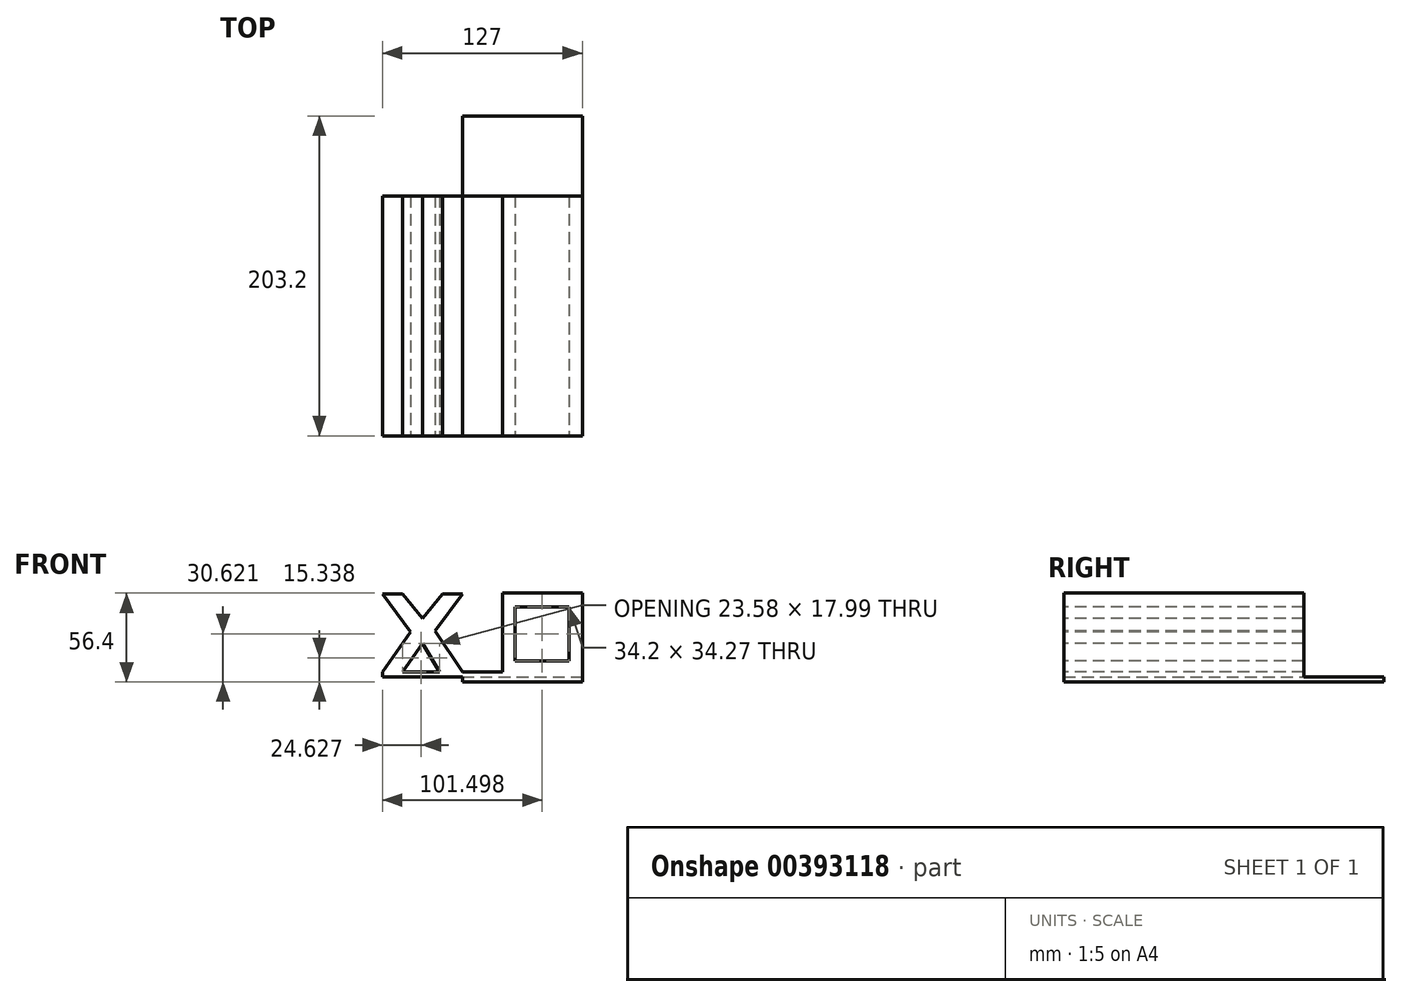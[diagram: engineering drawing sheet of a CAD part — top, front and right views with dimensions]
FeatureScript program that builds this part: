
annotation { "Feature Type Name" : "Feature", "Feature Type Description" : "" }
export const myFeature = defineFeature(function(context is Context, id is Id, definition is map)
    precondition{}
    {
        {
            var Q0;
            Q0=qCreatedBy(makeId("Top.planeOp"),FACE);
            var sketch = newSketch(context, id + "F0", { "sketchPlane" : qUnion([Q0])});
            skLineSegment(sketch, "E0.bottom", {"start": v(101.6, -101.6) * mm, "end": v(-101.6, -101.6) * mm});
            skLineSegment(sketch, "E0.top", {"start": v(101.6, 101.6) * mm, "end": v(-101.6, 101.6) * mm});
            skLineSegment(sketch, "E0.left", {"start": v(101.6, -101.6) * mm, "end": v(101.6, 101.6) * mm});
            skLineSegment(sketch, "E0.right", {"start": v(-101.6, -101.6) * mm, "end": v(-101.6, 101.6) * mm});
            skPoint(sketch, "E0.middle", {"position": v(0, 0) * mm});
            skSolve(sketch);
        }
        {
            var Q0;
            Q0=makeQuery(id+"F0.imprint","IMPRINT",FACE,{"disambiguationData":[TD([[makeQuery(id+"F0.imprint","IMPRINT",EDGE,{"derivedFrom":sQuery(id+"F0.wireOp",EDGE,"E0.bottom")}),-1.0]])]});
            extrude(context, id + "F1", {"entities" : qUnion([Q0]), "depth" : 6.35 * mm});
        }
        {
            var Q0;
            Q0=makeQuery(id+"F1.opExtrude","CAP_FACE",FACE,{"disambiguationData":[OSD([sQuery(id+"F0.wireOp",EDGE,"E0.bottom"),sQuery(id+"F0.wireOp",EDGE,"E0.top"),sQuery(id+"F0.wireOp",EDGE,"E0.left"),sQuery(id+"F0.wireOp",EDGE,"E0.right")])],"isStart":false});
            var sketch = newSketch(context, id + "F2", { "sketchPlane" : qUnion([Q0])});
            skLineSegment(sketch, "E1.bottom", {"start": v(-105.25, 101.6) * mm, "end": v(123.35, 101.6) * mm});
            skLineSegment(sketch, "E1.top", {"start": v(-105.25, 50.8) * mm, "end": v(123.35, 50.8) * mm});
            skLineSegment(sketch, "E1.left", {"start": v(-105.25, 101.6) * mm, "end": v(-105.25, 50.8) * mm});
            skLineSegment(sketch, "E1.right", {"start": v(123.35, 101.6) * mm, "end": v(123.35, 50.8) * mm});
            skSolve(sketch);
        }
        {
            var Q0;
            Q0=qSketchRegion(id+"F2",true);
            extrude(context, id + "F3", {"entities" : qUnion([Q0]), "operationType" : NewBodyOperationType.REMOVE, "oppositeDirection" : true, "depth" : 3.17 * mm});
        }
        {
            var Q0;
            Q0=qCreatedBy(makeId("Front.planeOp"),FACE);
            var sketch = newSketch(context, id + "F4", { "sketchPlane" : qUnion([Q0])});
            skLineSegment(sketch, "E2.bottom", {"start": v(101.6, 5.6) * mm, "end": v(50.8, 5.6) * mm});
            skLineSegment(sketch, "E2.top", {"start": v(101.6, 56.4) * mm, "end": v(50.8, 56.4) * mm});
            skLineSegment(sketch, "E2.left", {"start": v(101.6, 5.6) * mm, "end": v(101.6, 56.4) * mm});
            skLineSegment(sketch, "E2.right", {"start": v(50.8, 5.6) * mm, "end": v(50.8, 56.4) * mm});
            skSolve(sketch);
        }
        {
            var Q0;
            Q0=makeQuery(id+"F4.imprint","IMPRINT",FACE,{"disambiguationData":[TD([[makeQuery(id+"F4.imprint","IMPRINT",EDGE,{"derivedFrom":sQuery(id+"F4.wireOp",EDGE,"E2.bottom")}),-1.0]])]});
            extrude(context, id + "F5", {"entities" : qUnion([Q0]), "operationType" : NewBodyOperationType.ADD, "depth" : 101.6 * mm});
        }
        {
            var Q0;
            Q0=makeQuery(id+"F5.boolean.opBoolean","MERGE",FACE,{"derivedFrom":[makeQuery(id+"FEnlMJxP7i9bCVA_1.boolean.opBoolean","MERGE",FACE,{"derivedFrom":[makeQuery(id+"F2wCx2niY0FLEcg_1.boolean.opBoolean","MERGE",FACE,{"derivedFrom":[makeQuery(id+"F1.opExtrude","SWEPT_FACE",FACE,{"disambiguationData":[OSD([sQuery(id+"F0.wireOp",EDGE,"E0.bottom")])]}),makeQuery(id+"F2wCx2niY0FLEcg_1.opExtrude","CAP_FACE",FACE,{"disambiguationData":[OSD([sQuery(id+"FKLyXyjaw4T679Z_1.wireOp",EDGE,"gtplRE7N-Sajm-jqsF-KV1v-MEJ2AHi3Lrlc"),sQuery(id+"FKLyXyjaw4T679Z_1.wireOp",EDGE,"gQj6qFVv-T5yL-aiiH-ByfY-nZvvdH7kWqXa"),sQuery(id+"FKLyXyjaw4T679Z_1.wireOp",EDGE,"ks7bjJZl-BRkW-OQzJ-TQNI-whPCYHBAknJJ")])],"isStart":false})]}),makeQuery(id+"FEnlMJxP7i9bCVA_1.opExtrude","CAP_FACE",FACE,{"disambiguationData":[OSD([sQuery(id+"F7mE1Dz3g90iUiG_1.wireOp",EDGE,"W6MNkJQe-929A-tBjn-a2kg-PFGQEftXz8sj")])],"isStart":false})]}),makeQuery(id+"F5.opExtrude","CAP_FACE",FACE,{"disambiguationData":[OSD([sQuery(id+"F4.wireOp",EDGE,"E2.bottom"),sQuery(id+"F4.wireOp",EDGE,"E2.top"),sQuery(id+"F4.wireOp",EDGE,"E2.left"),sQuery(id+"F4.wireOp",EDGE,"E2.right")])],"isStart":false})]});
            var sketch = newSketch(context, id + "F6", { "sketchPlane" : qUnion([Q0])});
            skLineSegment(sketch, "E3.bottom", {"start": v(59, 13.49) * mm, "end": v(93.2, 13.49) * mm});
            skLineSegment(sketch, "E3.top", {"start": v(59, 47.76) * mm, "end": v(93.2, 47.76) * mm});
            skLineSegment(sketch, "E3.left", {"start": v(59, 13.49) * mm, "end": v(59, 47.76) * mm});
            skLineSegment(sketch, "E3.right", {"start": v(93.2, 13.49) * mm, "end": v(93.2, 47.76) * mm});
            skSolve(sketch);
        }
        {
            var Q0;
            Q0 = qSketchRegion(id + "F4", true);
            extrude(context, id + "F7", {"entities" : qUnion([Q0]), "operationType" : NewBodyOperationType.ADD, "oppositeDirection" : true, "depth" : 50.8 * mm});
        }
        {
            var Q0;
            Q0=makeQuery(id+"F6.imprint","IMPRINT",FACE,{"disambiguationData":[TD([[makeQuery(id+"F6.imprint","IMPRINT",EDGE,{"derivedFrom":sQuery(id+"F6.wireOp",EDGE,"E3.bottom")}),1.0]])]});
            extrude(context, id + "F8", {"entities" : qUnion([Q0]), "operationType" : NewBodyOperationType.REMOVE, "oppositeDirection" : true, "depth" : 203.2 * mm});
        }
        {
            var Q0;
            Q0=qCreatedBy(makeId("Front.planeOp"),FACE);
            var sketch = newSketch(context, id + "F9", { "sketchPlane" : qUnion([Q0])});
            skLineSegment(sketch, "E4.bottom", {"start": v(25.43, 5.03) * mm, "end": v(-25.37, 5.03) * mm});
            skLineSegment(sketch, "E4.top", {"start": v(25.43, 55.83) * mm, "end": v(-25.37, 55.83) * mm});
            skLineSegment(sketch, "E4.left", {"start": v(25.43, 5.03) * mm, "end": v(25.43, 55.83) * mm});
            skLineSegment(sketch, "E4.right", {"start": v(-25.37, 5.03) * mm, "end": v(-25.37, 55.83) * mm});
            skSolve(sketch);
        }
        {
            var Q0;
            Q0=makeQuery(id+"F9.imprint","IMPRINT",FACE,{"disambiguationData":[TD([[makeQuery(id+"F9.imprint","IMPRINT",EDGE,{"derivedFrom":sQuery(id+"F9.wireOp",EDGE,"E4.bottom")}),-1.0]])]});
            extrude(context, id + "F10", {"entities" : qUnion([Q0]), "operationType" : NewBodyOperationType.ADD, "depth" : 101.6 * mm});
        }
        {
            var Q0;
            Q0=makeQuery(id+"F10.opExtrude","CAP_FACE",FACE,{"disambiguationData":[OSD([sQuery(id+"F9.wireOp",EDGE,"E4.bottom"),sQuery(id+"F9.wireOp",EDGE,"E4.top"),sQuery(id+"F9.wireOp",EDGE,"E4.left"),sQuery(id+"F9.wireOp",EDGE,"E4.right")])],"isStart":true});
            extrude(context, id + "F11", {"entities" : qUnion([Q0]), "operationType" : NewBodyOperationType.ADD, "depth" : 50.8 * mm});
        }
        {
            var Q0;
            Q0=makeQuery(id+"F1.opExtrude","CAP_FACE",FACE,{"disambiguationData":[OSD([sQuery(id+"F0.wireOp",EDGE,"E0.bottom"),sQuery(id+"F0.wireOp",EDGE,"E0.top"),sQuery(id+"F0.wireOp",EDGE,"E0.left"),sQuery(id+"F0.wireOp",EDGE,"E0.right")])],"isStart":true});
            var sketch = newSketch(context, id + "F12", { "sketchPlane" : qUnion([Q0])});
            skLineSegment(sketch, "E5.bottom", {"start": v(-101.6, 101.6) * mm, "end": v(-25.4, 101.6) * mm});
            skLineSegment(sketch, "E5.top", {"start": v(-101.6, -101.6) * mm, "end": v(-25.4, -101.6) * mm});
            skLineSegment(sketch, "E5.left", {"start": v(-101.6, 101.6) * mm, "end": v(-101.6, -101.6) * mm});
            skLineSegment(sketch, "E5.right", {"start": v(-25.4, 101.6) * mm, "end": v(-25.4, -101.6) * mm});
            skSolve(sketch);
        }
        {
            var Q0;
            Q0=makeQuery(id+"F12.imprint","IMPRINT",FACE,{"disambiguationData":[TD([[makeQuery(id+"F12.imprint","IMPRINT",EDGE,{"derivedFrom":sQuery(id+"F12.wireOp",EDGE,"E5.bottom")}),1.0]])]});
            extrude(context, id + "F13", {"entities" : qUnion([Q0]), "operationType" : NewBodyOperationType.REMOVE, "oppositeDirection" : true, "depth" : 25.4 * mm});
        }
        {
            var Q0;
            Q0=makeQuery(id+"F1.opExtrude","CAP_FACE",FACE,{"disambiguationData":[OSD([sQuery(id+"F0.wireOp",EDGE,"E0.bottom"),sQuery(id+"F0.wireOp",EDGE,"E0.top"),sQuery(id+"F0.wireOp",EDGE,"E0.left"),sQuery(id+"F0.wireOp",EDGE,"E0.right")])],"isStart":true});
            var sketch = newSketch(context, id + "F14", { "sketchPlane" : qUnion([Q0])});
            skLineSegment(sketch, "E6.bottom", {"start": v(-25.4, 101.6) * mm, "end": v(25.4, 101.6) * mm});
            skLineSegment(sketch, "E6.top", {"start": v(-25.4, -101.6) * mm, "end": v(25.4, -101.6) * mm});
            skLineSegment(sketch, "E6.left", {"start": v(-25.4, 101.6) * mm, "end": v(-25.4, -101.6) * mm});
            skLineSegment(sketch, "E6.right", {"start": v(25.4, 101.6) * mm, "end": v(25.4, -101.6) * mm});
            skSolve(sketch);
        }
        {
            var Q0;
            Q0=makeQuery(id+"F10.boolean.opBoolean","MERGE",FACE,{"derivedFrom":[makeQuery(id+"F5.boolean.opBoolean","MERGE",FACE,{"derivedFrom":[makeQuery(id+"F1.opExtrude","SWEPT_FACE",FACE,{"disambiguationData":[OSD([sQuery(id+"F0.wireOp",EDGE,"E0.bottom")])]}),makeQuery(id+"F5.opExtrude","CAP_FACE",FACE,{"disambiguationData":[OSD([sQuery(id+"F4.wireOp",EDGE,"E2.bottom"),sQuery(id+"F4.wireOp",EDGE,"E2.top"),sQuery(id+"F4.wireOp",EDGE,"E2.left"),sQuery(id+"F4.wireOp",EDGE,"E2.right")])],"isStart":false})]}),makeQuery(id+"F10.opExtrude","CAP_FACE",FACE,{"disambiguationData":[OSD([sQuery(id+"F9.wireOp",EDGE,"E4.bottom"),sQuery(id+"F9.wireOp",EDGE,"E4.top"),sQuery(id+"F9.wireOp",EDGE,"E4.left"),sQuery(id+"F9.wireOp",EDGE,"E4.right")])],"isStart":false})]});
            var sketch = newSketch(context, id + "F15", { "sketchPlane" : qUnion([Q0])});
            skLineSegment(sketch, "E7", {"start": v(-25.37, 55.83) * mm, "end": v(-7.65, 31.72) * mm});
            skLineSegment(sketch, "E8", {"start": v(-7.65, 31.72) * mm, "end": v(-25.37, 6.35) * mm});
            skLineSegment(sketch, "E9", {"start": v(-25.37, 6.35) * mm, "end": v(-12.56, 6.35) * mm});
            skLineSegment(sketch, "E10", {"start": v(-12.56, 6.35) * mm, "end": v(0, 24.33) * mm});
            skLineSegment(sketch, "E11", {"start": v(0, 24.33) * mm, "end": v(11, 6.35) * mm});
            skLineSegment(sketch, "E12", {"start": v(11, 6.35) * mm, "end": v(25.43, 6.35) * mm});
            skLineSegment(sketch, "E13", {"start": v(25.43, 6.35) * mm, "end": v(7.99, 32.29) * mm});
            skLineSegment(sketch, "E14", {"start": v(7.99, 32.29) * mm, "end": v(25.43, 55.83) * mm});
            skLineSegment(sketch, "E15", {"start": v(25.43, 55.83) * mm, "end": v(12.7, 55.83) * mm});
            skLineSegment(sketch, "E16", {"start": v(12.7, 55.83) * mm, "end": v(0, 40.48) * mm});
            skLineSegment(sketch, "E17", {"start": v(0, 40.48) * mm, "end": v(-12.51, 55.83) * mm});
            skLineSegment(sketch, "E18", {"start": v(-12.51, 55.83) * mm, "end": v(-25.37, 55.83) * mm});
            skSolve(sketch);
        }
        {
            var Q0;
            Q0=makeQuery(id+"F15.imprint","IMPRINT",FACE,{"disambiguationData":[TD([[makeQuery(id+"F15.imprint","IMPRINT",EDGE,{"derivedFrom":sQuery(id+"F15.wireOp",EDGE,"E9")}),-1.0]])]});
            var sketch = newSketch(context, id + "F16", { "sketchPlane" : qUnion([Q0])});
            skLineSegment(sketch, "E19", {"start": v(-12.56, 6.34) * mm, "end": v(11.01, 6.34) * mm});
            skLineSegment(sketch, "E20", {"start": v(11.01, 6.34) * mm, "end": v(0, 24.33) * mm});
            skLineSegment(sketch, "E21", {"start": v(0, 24.33) * mm, "end": v(-12.56, 6.34) * mm});
            skSolve(sketch);
        }
        {
            var Q0;
            Q0 = qSketchRegion(id + "F16", true);
            var Q1;
            Q1=makeQuery(id+"F15.imprint","IMPRINT",FACE,{"disambiguationData":[TD([[makeQuery(id+"F15.imprint","IMPRINT",EDGE,{"derivedFrom":sQuery(id+"F15.wireOp",EDGE,"E7")}),-1.0]])]});
            var Q2;
            {var subQ0=sQuery(id+"F15.wireOp",EDGE,"E16");Q2=makeQuery(id+"F15.imprint","IMPRINT",FACE,{"disambiguationData":[TD([[makeQuery(id+"F15.imprint","IMPRINT",EDGE,{"derivedFrom":subQ0}),-1.0]])]});}
            var Q3;
            Q3=makeQuery(id+"F15.imprint","IMPRINT",FACE,{"disambiguationData":[TD([[makeQuery(id+"F15.imprint","IMPRINT",EDGE,{"derivedFrom":sQuery(id+"F15.wireOp",EDGE,"E13")}),-1.0]])]});
            extrude(context, id + "F17", {"entities" : qUnion([Q0, Q1, Q2, Q3]), "operationType" : NewBodyOperationType.REMOVE, "oppositeDirection" : true, "depth" : 209.55 * mm});
        }
        {
            var Q0;
            Q0=makeQuery(id+"F14.imprint","IMPRINT",FACE,{"disambiguationData":[TD([[makeQuery(id+"F14.imprint","IMPRINT",EDGE,{"derivedFrom":sQuery(id+"F14.wireOp",EDGE,"E6.bottom")}),1.0]])]});
            extrude(context, id + "F18", {"entities" : qUnion([Q0]), "operationType" : NewBodyOperationType.REMOVE, "oppositeDirection" : true, "depth" : 3.17 * mm});
        }
    });
